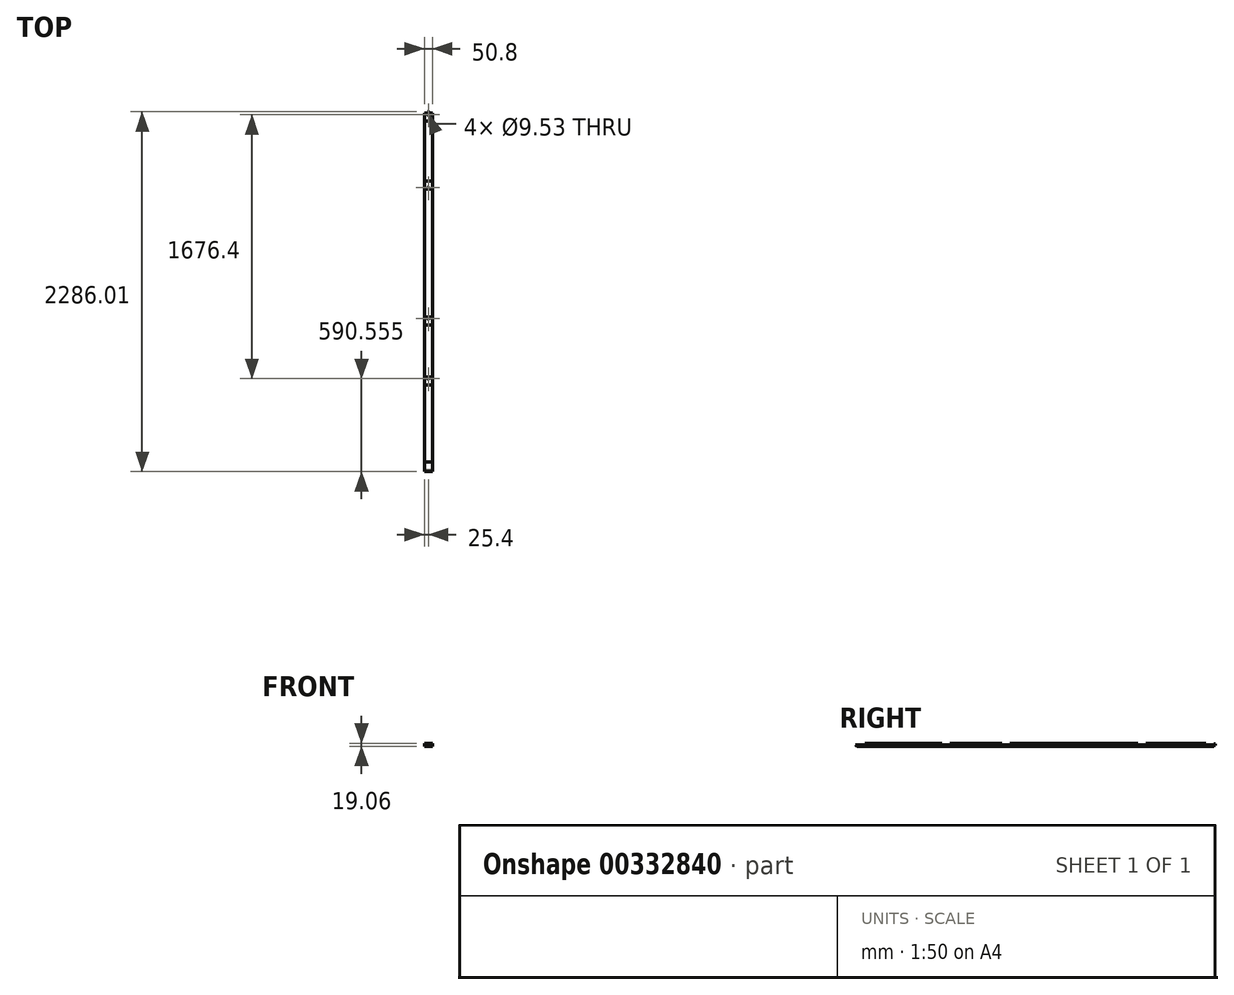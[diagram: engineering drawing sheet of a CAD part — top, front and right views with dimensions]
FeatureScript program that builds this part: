
annotation { "Feature Type Name" : "Feature", "Feature Type Description" : "" }
export const myFeature = defineFeature(function(context is Context, id is Id, definition is map)
    precondition{}
    {
        {
            var Q0;
            Q0=qCreatedBy(makeId("Right.planeOp"),FACE);
            var sketch = newSketch(context, id + "F0", { "sketchPlane" : qUnion([Q0])});
            skLineSegment(sketch, "E0.top", {"start": v(2133.6, -9.52) * mm, "end": v(2133.6, 0) * mm});
            skLineSegment(sketch, "E0.right", {"start": v(0, 9.52) * mm, "end": v(406.4, 9.53) * mm});
            skLineSegment(sketch, "E1.top", {"start": v(2082.8, 9.53) * mm, "end": v(2082.8, 0) * mm});
            skLineSegment(sketch, "E1.right", {"start": v(2133.6, 0) * mm, "end": v(2082.8, 0) * mm});
            skLineSegment(sketch, "E2", {"start": v(2133.6, -9.52) * mm, "end": v(-33.3, -9.53) * mm});
            skLineSegment(sketch, "E3.right", {"start": v(2082.8, 0) * mm, "end": v(2082.8, 0) * mm});
            skLineSegment(sketch, "E4.trimOffspring", {"start": v(2082.8, 9.53) * mm, "end": v(2082.8, 9.53) * mm});
            skLineSegment(sketch, "E5.top", {"start": v(1651, 9.53) * mm, "end": v(1651, 0) * mm});
            skLineSegment(sketch, "E5.right", {"start": v(1701.8, 0) * mm, "end": v(1651, 0) * mm});
            skLineSegment(sketch, "E6.bottom", {"start": v(838.2, 9.53) * mm, "end": v(838.2, 0) * mm});
            skLineSegment(sketch, "E6.top", {"start": v(787.4, 9.53) * mm, "end": v(787.4, 0) * mm});
            skLineSegment(sketch, "E6.right", {"start": v(838.2, 0) * mm, "end": v(787.4, 0) * mm});
            skPoint(sketch, "E6.left.start.orphan", {"position": v(838.2, 48.5) * mm});
            skPoint(sketch, "E7.orphan", {"position": v(787.4, 48.5) * mm});
            skLineSegment(sketch, "E8.trimOffspring", {"start": v(838.2, 9.53) * mm, "end": v(1651, 9.53) * mm});
            skLineSegment(sketch, "E9", {"start": v(1701.8, 0) * mm, "end": v(1701.8, 9.53) * mm});
            skLineSegment(sketch, "E10.trimOffspring", {"start": v(1701.8, 9.53) * mm, "end": v(2082.8, 9.53) * mm});
            skLineSegment(sketch, "E11", {"start": v(0, 9.52) * mm, "end": v(-82.55, 9.52) * mm});
            skLineSegment(sketch, "E12", {"start": v(-142.88, 0) * mm, "end": v(-133.35, -9.53) * mm});
            skLineSegment(sketch, "E13", {"start": v(-33.3, -9.53) * mm, "end": v(-133.35, -9.53) * mm});
            skPoint(sketch, "E14.start.orphan", {"position": v(431.8, 9.53) * mm});
            skLineSegment(sketch, "E15.top", {"start": v(406.4, 0) * mm, "end": v(457.2, 0) * mm});
            skLineSegment(sketch, "E15.left", {"start": v(406.4, 9.53) * mm, "end": v(406.4, 0) * mm});
            skLineSegment(sketch, "E15.right", {"start": v(457.2, 9.53) * mm, "end": v(457.2, 0) * mm});
            skLineSegment(sketch, "E16.trimOffspring", {"start": v(457.2, 9.53) * mm, "end": v(787.4, 9.53) * mm});
            skLineSegment(sketch, "E17.top", {"start": v(-142.88, 0) * mm, "end": v(-82.55, 0) * mm});
            skLineSegment(sketch, "E17.right", {"start": v(-82.55, 9.52) * mm, "end": v(-82.55, 0) * mm});
            skPoint(sketch, "E18.orphan", {"position": v(-152.4, 9.52) * mm});
            skSolve(sketch);
        }
        {
            var Q0;
            Q0=qSketchRegion(id+"F0",true);
            extrude(context, id + "F1", {"entities" : qUnion([Q0]), "endBound" : BoundingType.SYMMETRIC, "depth" : 50.8 * mm});
        }
        {
            var Q0;
            Q0=qCreatedBy(makeId("Front.planeOp"),FACE);
            cPlane(context, id + "F2", {"entities" : qUnion([Q0]), "cplaneType" : CPlaneType.OFFSET, "offset" : 2133.6 * mm, "oppositeDirection" : true, "width" : 152.4 * mm, "height" : 152.4 * mm});
        }
        {
            var Q0;
            Q0=qCreatedBy(id+"F2.planeOp",FACE);
            var sketch = newSketch(context, id + "F3", { "sketchPlane" : qUnion([Q0])});
            skCircle(sketch, "E19", {"center": v(0, 0) * mm, "radius": 4.76 * mm});
            skSolve(sketch);
        }
        {
            var Q0;
            Q0=qSketchRegion(id+"F3",true);
            extrude(context, id + "F4", {"entities" : qUnion([Q0]), "operationType" : NewBodyOperationType.ADD, "oppositeDirection" : true, "depth" : 9.52 * mm});
        }
        {
            var Q0;
            Q0=qCreatedBy(makeId("Top.planeOp"),FACE);
            var sketch = newSketch(context, id + "F5", { "sketchPlane" : qUnion([Q0])});
            skCircle(sketch, "E20", {"center": v(0, 447.67) * mm, "radius": 4.76 * mm});
            skCircle(sketch, "E21", {"center": v(0, 828.67) * mm, "radius": 4.76 * mm});
            skCircle(sketch, "E22", {"center": v(0, 1660.52) * mm, "radius": 4.76 * mm});
            skCircle(sketch, "E23", {"center": v(0, 2124.07) * mm, "radius": 4.76 * mm});
            skSolve(sketch);
        }
        {
            var Q0;
            Q0 = qSketchRegion(id + "F5", true);
            extrude(context, id + "F6", {"entities" : qUnion([Q0]), "operationType" : NewBodyOperationType.REMOVE, "oppositeDirection" : true, "depth" : 25.4 * mm});
        }
    });
